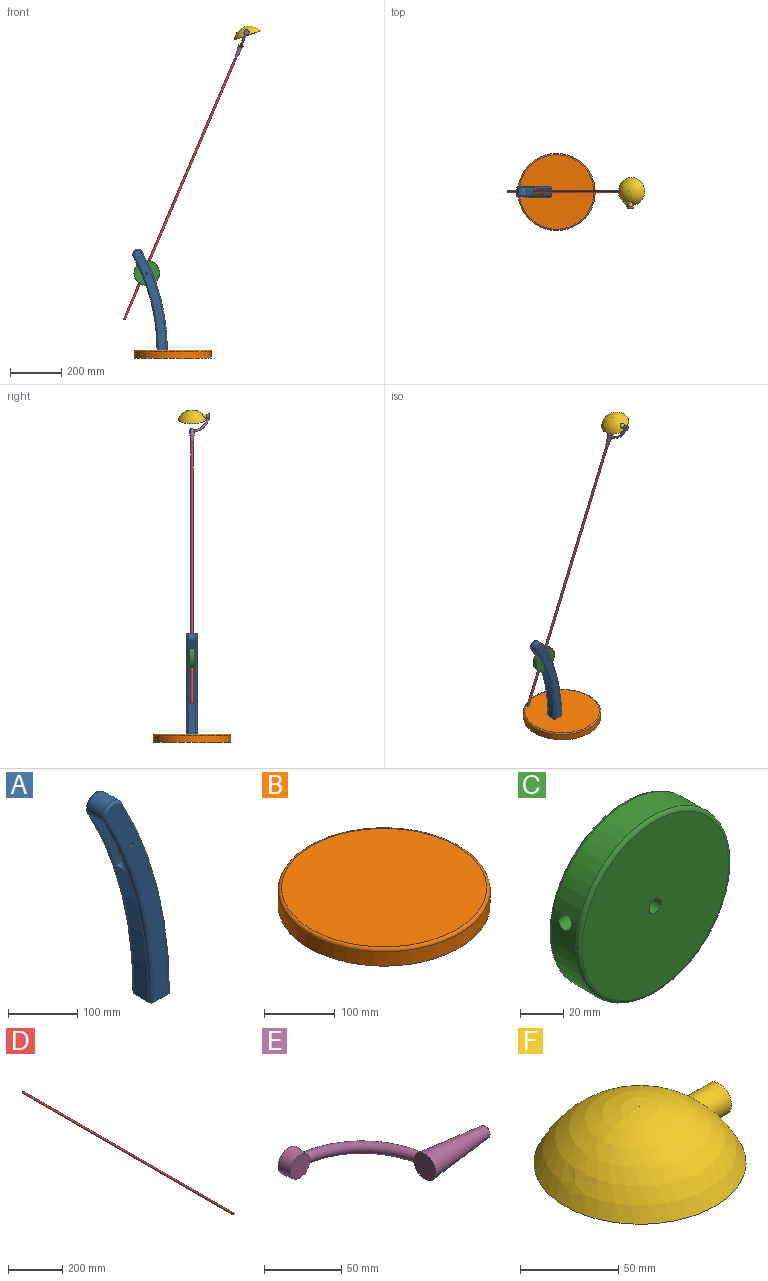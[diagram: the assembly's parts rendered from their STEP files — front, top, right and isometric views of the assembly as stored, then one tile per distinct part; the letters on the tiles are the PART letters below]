
ASSEMBLY  parts=6 mates=5
PART A: 18 faces, bbox 202.3x40x413.6 mm
  f0: cylinder r=760mm len=363mm, axis (0,-1,0), area 9543.7mm2, adj f1,f5,f6,f7,f8,f9,f13,f17
  f1: plane 40x40mm, normal (0,0,-1), area 1578.5mm2, adj f0,f2,f3,f4,f12,f13,f15,f17
  f2: cylinder r=800mm len=382.1mm, axis (0,-1,0), area 10094.3mm2, adj f1,f5,f6,f7,f8,f9,f12,f15
  f3: plane 387.55x124.72mm, normal (0,1,0), area 11955.3mm2, adj f1,f11,f15,f16,f17
  f4: plane 387.55x124.72mm, normal (0,-1,0), area 11955.3mm2, adj f1,f10,f12,f13,f14
  f5: cylinder r=20mm len=37.57mm, axis (0,-1,0), area 1885mm2, adj f0,f2,f14,f16
  f6: cylinder r=50mm len=37.38mm, axis (0,-1,0), area 823.4mm2, adj f0,f2,f8,f9
  f7: cylinder r=50mm len=36.47mm, axis (0,-1,0), area 823.4mm2, adj f0,f2,f8,f9
  f8: plane 100x72.16mm, normal (0,-1,0), area 3840.9mm2, adj f0,f2,f6,f7,f11
  f9: plane 100x72.16mm, normal (0,1,0), area 3840.9mm2, adj f0,f2,f6,f7,f10
  f10: cylinder r=4mm len=10mm, axis (0,-1,0), area 251.3mm2, adj f4,f9
  f11: cylinder r=4mm len=10mm, axis (0,-1,0), area 251.3mm2, adj f3,f8
  f12: torus R=795mm, axis (0,-1,0), area 3121.6mm2, adj f1,f2,f4,f14
  f13: torus R=765mm, axis (0,-1,0), area 2979.4mm2, adj f0,f1,f4,f14
  f14: torus R=15mm, axis (0,-1,0), area 448.6mm2, adj f4,f5,f12,f13
  f15: torus R=795mm, axis (0,-1,0), area 3121.6mm2, adj f1,f2,f3,f16
  f16: torus R=15mm, axis (0,-1,0), area 448.6mm2, adj f3,f5,f15,f17
  f17: torus R=765mm, axis (0,-1,0), area 2979.4mm2, adj f0,f1,f3,f16
PART B: 4 faces, bbox 324.7x324.7x30 mm
  f0: cylinder r=150mm len=300mm, axis (0,0,-1), area 23561.9mm2, adj f2,f3
  f1: plane 290x290mm, normal (0,0,1), area 66052mm2, adj f3
  f2: plane 300x300mm, normal (0,0,-1), area 70685.8mm2, adj f0
  f3: torus R=145mm, axis (0,0,1), area 7312.5mm2, adj f0,f1
PART C: 7 faces, bbox 108.2x20x108.2 mm
  f0: cylinder r=50mm len=100mm, axis (0,1,0), area 4923.2mm2, adj f3,f4,f5
  f1: plane 96x96mm, normal (0,-1,0), area 7188mm2, adj f4,f6
  f2: plane 96x96mm, normal (0,1,0), area 7188mm2, adj f3,f6
  f3: torus R=48mm, axis (0,-1,0), area 972.6mm2, adj f0,f2
  f4: torus R=48mm, axis (0,-1,0), area 972.6mm2, adj f0,f1
  f5: cylinder r=4mm len=99.28mm, axis (1,0,0), area 2458.2mm2, adj f0
  f6: cylinder r=4mm len=20mm, axis (0,-1,0), area 502.7mm2, adj f1,f2
PART D: 3 faces, bbox 8x1100x8 mm
  f0: cylinder r=4mm len=1100mm, axis (0,1,0), area 27646mm2, adj f1,f2
  f1: plane 8x8mm, normal (0,-1,0), area 50.3mm2, adj f0
  f2: plane 8x8mm, normal (0,1,0), area 50.3mm2, adj f0
PART E: 7 faces, bbox 122x80.8x20 mm
  f0: plane 20x20mm, normal (0,1,0), area 314.2mm2, adj f2
  f1: plane 18x18mm, normal (0,-1,0), area 254.5mm2, adj f2
  f2: cone r=9mm half-angle=5.7deg, axis (0,1,0), area 548.4mm2, adj f0,f1,f3
  f3: torus R=62mm, axis (0,0,-1), area 1990.3mm2, adj f2,f6
  f4: plane 9x9mm, normal (1,0,0), area 63.6mm2, adj f6
  f5: plane 20x20mm, normal (-1,0,0), area 314.2mm2, adj f6
  f6: cone r=4.5mm half-angle=5.7deg, axis (-1,0,0), area 2464.8mm2, adj f3,f4,f5
PART F: 4 faces, bbox 111x108x35 mm
  f0: sphere r=59.16mm, area 12682.8mm2, adj f1,f2
  f1: plane 108x108mm, normal (0,0,-1), area 9160.9mm2, adj f0
  f2: cylinder r=9mm len=18.79mm, axis (-1,0,0), area 640.9mm2, adj f0,f3
  f3: plane 18x18mm, normal (1,0,0), area 254.5mm2, adj f2
PLACE A t=(-819.77,0.12,9.97)mm
PLACE B t=(0.23,0.12,-20.03)mm fixed
PLACE C rot(axis=(0,-1,0),66.9deg) t=(-99.77,0.12,309.97)mm
PLACE D rot(axis=(-0.96,0.2,0.2),92.3deg) t=(28.14,0.12,635.66)mm
PLACE E rot(axis=(0.55,0,-0.83),180deg) t=(263.35,0.12,1187.64)mm
PLACE F rot(axis=(0.16,-0.16,-0.97),91.6deg) t=(291.56,0.12,1233.33)mm
MATE fastened A.f1 <-> B.f1  axis (0,0,-1) through (-39.77,0.12,9.97)mm
MATE revolute C.f0 <-> A.f6  axis (0,1,0) through (-99.77,10.12,309.97)mm
MATE fastened E.f6 <-> D.f0  axis (-0.39,0,-0.92) through (243.75,0.12,1141.64)mm
MATE revolute F.f2 <-> E.f2  axis (0,-1,0) through (287.66,-56.88,1244.67)mm
MATE fastened D.f0 <-> C.f5  axis (-0.39,0,-0.92) through (-187.47,0.12,129.68)mm
